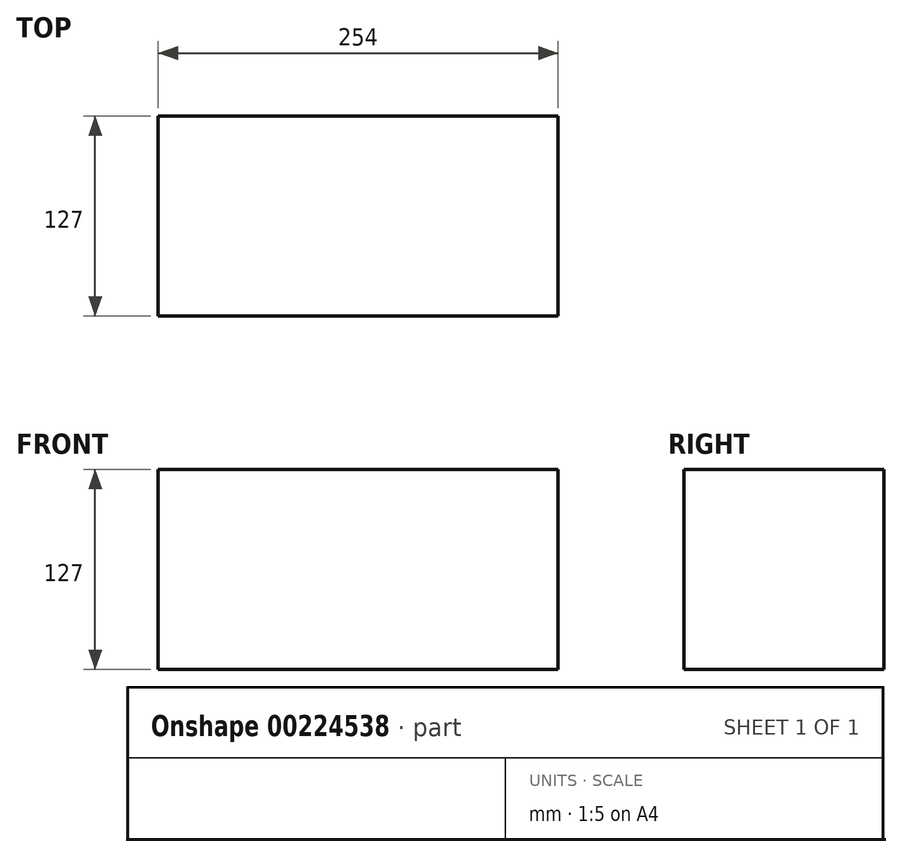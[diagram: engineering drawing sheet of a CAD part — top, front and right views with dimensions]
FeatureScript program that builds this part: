
annotation { "Feature Type Name" : "Feature", "Feature Type Description" : "" }
export const myFeature = defineFeature(function(context is Context, id is Id, definition is map)
    precondition{}
    {
        {
            var Q0;
            Q0=qCreatedBy(makeId("Front.planeOp"),FACE);
            var sketch = newSketch(context, id + "F0", { "sketchPlane" : qUnion([Q0])});
            skLineSegment(sketch, "E0.bottom", {"start": v(-130.86, 11.93) * mm, "end": v(123.14, 11.93) * mm});
            skLineSegment(sketch, "E0.top", {"start": v(-130.86, -115.07) * mm, "end": v(123.14, -115.07) * mm});
            skLineSegment(sketch, "E0.left", {"start": v(-130.86, 11.93) * mm, "end": v(-130.86, -115.07) * mm});
            skLineSegment(sketch, "E0.right", {"start": v(123.14, 11.93) * mm, "end": v(123.14, -115.07) * mm});
            skSolve(sketch);
        }
        {
            var Q0;
            Q0=makeQuery(id+"F0.imprint","IMPRINT",FACE,{"disambiguationData":[TD([[makeQuery(id+"F0.imprint","IMPRINT",EDGE,{"derivedFrom":sQuery(id+"F0.wireOp",EDGE,"E0.bottom")}),-1.0]])]});
            extrude(context, id + "F1", {"entities" : qUnion([Q0]), "depth" : 127 * mm});
        }
    });
